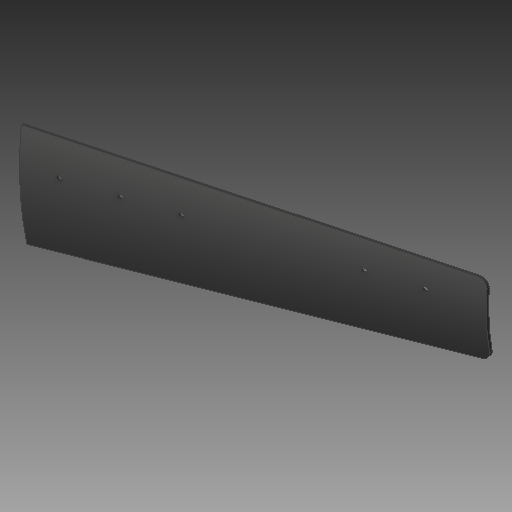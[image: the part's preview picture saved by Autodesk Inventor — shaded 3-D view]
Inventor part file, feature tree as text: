
AUTODESK INVENTOR PART (.ipt)
format: ipt  version: 2019 (Build 230136000, 136)  size: 171,520 bytes
history: native  units: mm
features: other x3, move_body x2, fillet x1, direct_edit x1
ambient origin geometry x8: Origin, YZ Plane, XZ Plane, XY Plane, X Axis, Y Axis, Z Axis, Center Point
bodies: Solid1 (feature_tree)
feature tree (7):
  other  "BladeSkeleton.ipt"
  fillet  "Fillet1"  Radius=10.0mm
  direct_edit  "Direct Edit1"
  other  "Solid2::BladeSkeleton.ipt"
  other  "TaggingFeature1"
  move_body  "Move1"
  move_body  "Move2"
